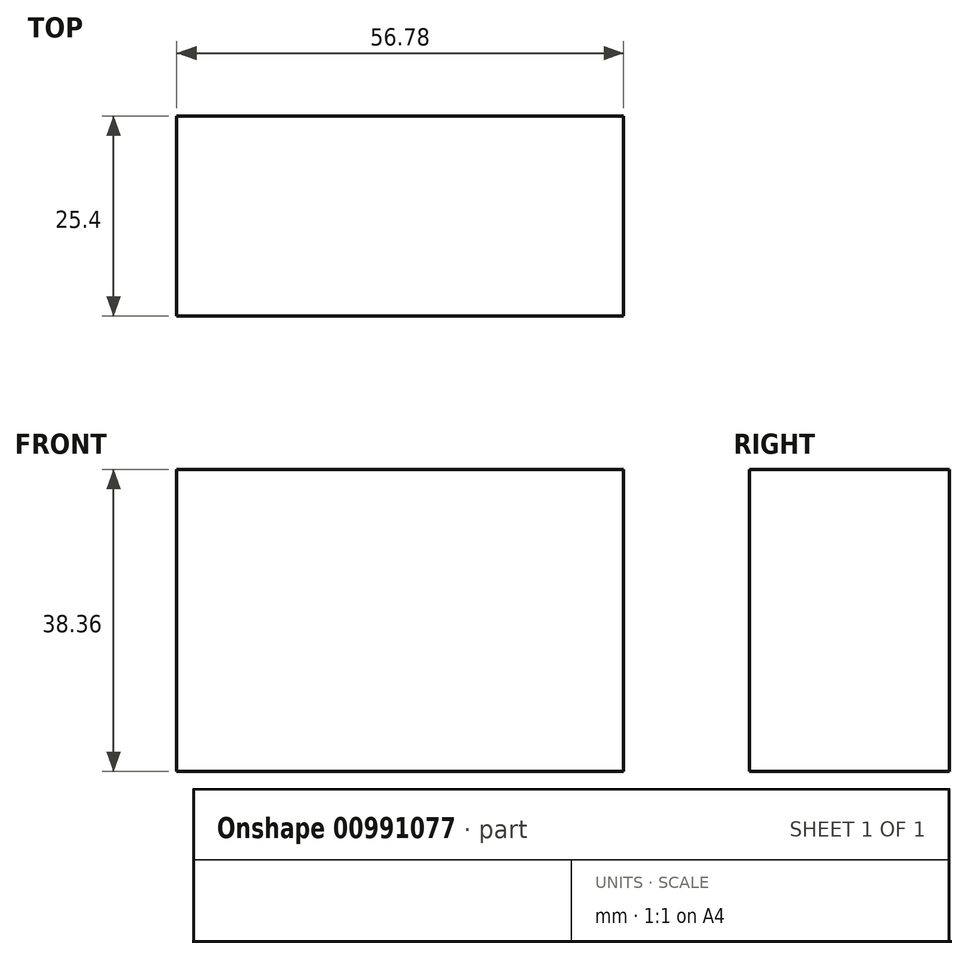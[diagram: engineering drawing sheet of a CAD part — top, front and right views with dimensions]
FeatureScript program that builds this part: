
annotation { "Feature Type Name" : "Feature", "Feature Type Description" : "" }
export const myFeature = defineFeature(function(context is Context, id is Id, definition is map)
    precondition{}
    {
        {
            var Q0;
            Q0=qCreatedBy(makeId("Front.planeOp"),FACE);
            var sketch = newSketch(context, id + "F0", { "sketchPlane" : qUnion([Q0])});
            skLineSegment(sketch, "E0.bottom", {"start": v(-97.48, 48.48) * mm, "end": v(-40.7, 48.48) * mm});
            skLineSegment(sketch, "E0.top", {"start": v(-97.48, 10.12) * mm, "end": v(-40.7, 10.12) * mm});
            skLineSegment(sketch, "E0.left", {"start": v(-97.48, 48.48) * mm, "end": v(-97.48, 10.12) * mm});
            skLineSegment(sketch, "E0.right", {"start": v(-40.7, 48.48) * mm, "end": v(-40.7, 10.12) * mm});
            skSolve(sketch);
        }
        {
            var Q0;
            Q0 = qSketchRegion(id + "F0", true);
            extrude(context, id + "F1", {"entities" : qUnion([Q0]), "depth" : 25.4 * mm, "offsetDistance" : 25.4 * mm});
        }
    });
